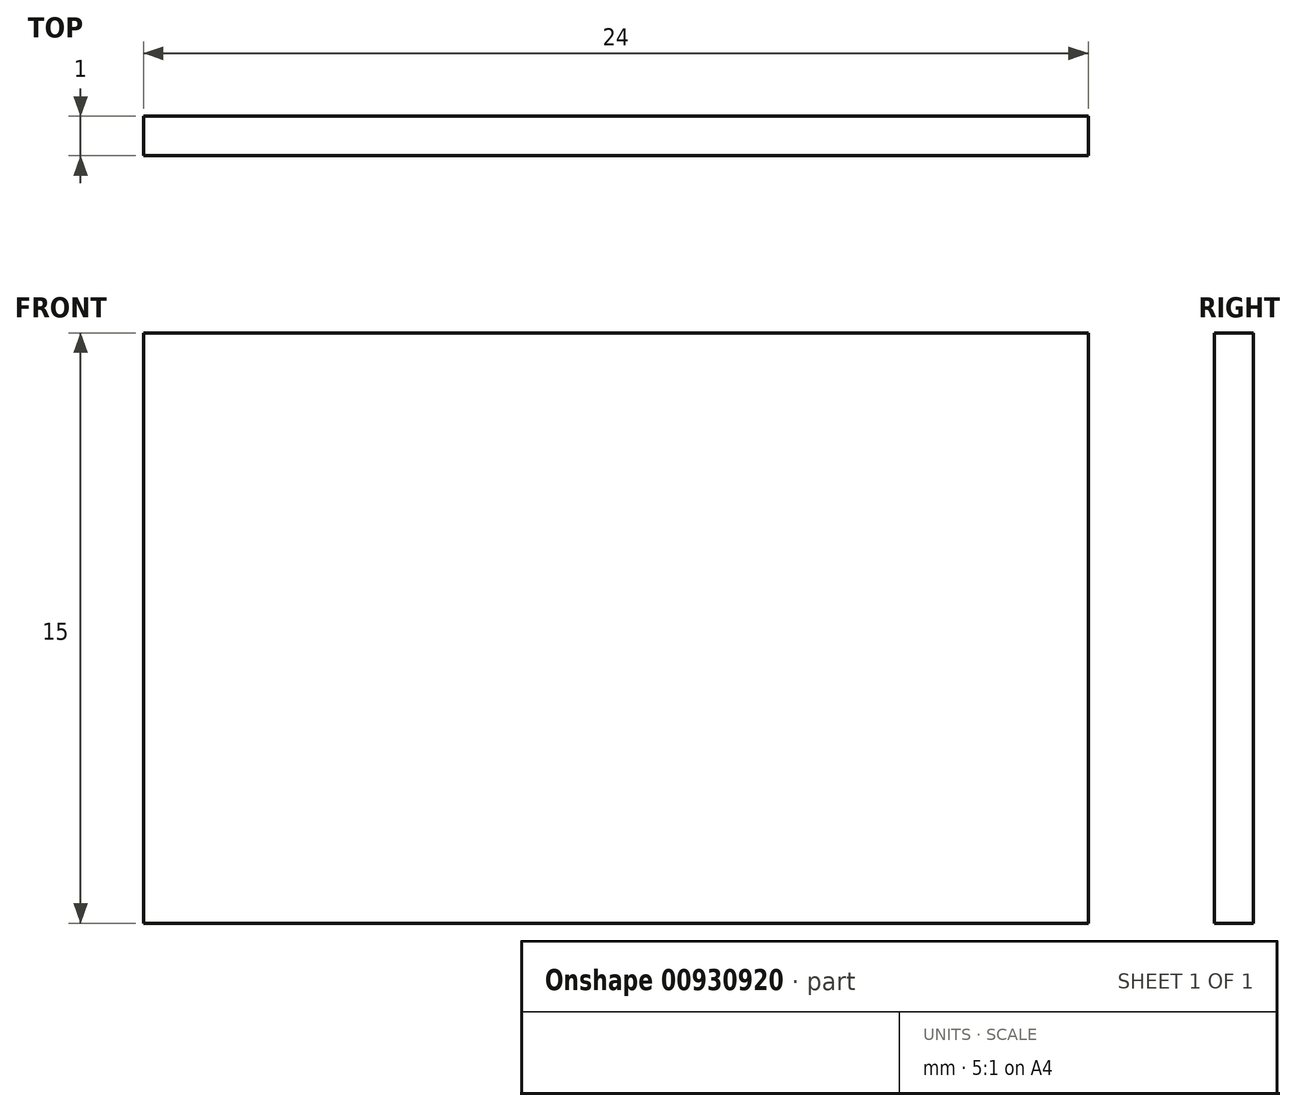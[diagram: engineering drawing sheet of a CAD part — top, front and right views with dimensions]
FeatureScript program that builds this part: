
annotation { "Feature Type Name" : "Feature", "Feature Type Description" : "" }
export const myFeature = defineFeature(function(context is Context, id is Id, definition is map)
    precondition{}
    {
        {
            var Q0;
            Q0=qCreatedBy(makeId("Front.planeOp"),FACE);
            var sketch = newSketch(context, id + "F0", { "sketchPlane" : qUnion([Q0])});
            skLineSegment(sketch, "E0.bottom", {"start": v(12, 7.5) * mm, "end": v(-12, 7.5) * mm});
            skLineSegment(sketch, "E0.top", {"start": v(12, -7.5) * mm, "end": v(-12, -7.5) * mm});
            skLineSegment(sketch, "E0.left", {"start": v(12, 7.5) * mm, "end": v(12, -7.5) * mm});
            skLineSegment(sketch, "E0.right", {"start": v(-12, 7.5) * mm, "end": v(-12, -7.5) * mm});
            skPoint(sketch, "E0.middle", {"position": v(0, 0) * mm});
            skSolve(sketch);
        }
        {
            var Q0;
            Q0=makeQuery(id+"F0.imprint","IMPRINT",FACE,{"disambiguationData":[TD([[makeQuery(id+"F0.imprint","IMPRINT",EDGE,{"derivedFrom":sQuery(id+"F0.wireOp",EDGE,"E0.bottom")}),1.0]])]});
            extrude(context, id + "F1", {"entities" : qUnion([Q0]), "depth" : 1 * mm, "offsetDistance" : 25 * mm});
        }
    });
